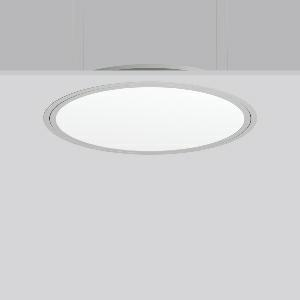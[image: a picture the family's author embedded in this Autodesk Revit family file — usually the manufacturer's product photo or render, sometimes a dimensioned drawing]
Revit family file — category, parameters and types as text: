
# Revit family: triona_round_e_312383_004_1_12_def9
name_source: partatom
category: Lighting Fixtures
units: mm (PartAtom-declared; Revit-internal decimal feet)

## family parameters
Cut with Voids When Loaded = No
Host = Face
Light Source = No
Part Type = Normal
Room Calculation Point = No
Round Connector Dimension = Use Diameter
Shared = No

## types (1)
- TRIONA round E (1 x LED Modul 840, 6750 lm, 4000)
    Apparent Load = 70 VA
    CIE Flux Codes = 49 80 96 100 100
    Color Rendering = 80
    Color Temperature = 4000
    Default Elevation = 1800 mm
    Description = Series: TRIONA round
Decorative round LED recessed surface luminaire. Cover made of sheet steel, powder-coated. Frame made of aluminium, powder-coated. Recessed ring: aluminium extrusion profile, powder coated. Light emission through a diffuser: plastic, opal. Lightguide and diffuser made of non-yellowing plastic (PMMA). Lateral light emission (RZB SIDELITE technology) for above-average homogeneous light distribution. Suitable for installation in cavity ceilings. Tool-free mounting system thanks to the rocker arm mechanism (patent pending). Electronic ballast included. Very easy installation thanks to Plug+Play connection. 
Colour: silver, matt (approx. RAL 9006)
Diameter: 725 mm
Height: 2 mm
Cut-out diameter: 702 mm
Recess height: 100 mm
Luminaire: recess height: 89 mm
Lamp: LED
Socket: without socket
Colour temperature: 4000K
Colour rendering index (CRI): 80
System power: 70 W
Rated luminous flux: 6750 lm
Luminous efficiency: 96 lm/W
Control gear: Converter, dimmable, DALI
Protection class: I
Type of protection: IP 40
    Height = 0 mm  [stored 0 ft]
    Lamp = 1 x LED Modul 840
    Lamp Light Flux = 6750 lm
    Lamp count = 1
    Length = 725 mm
    Lifetime = 50000 h
    Luminous efficacy = 96 lm/W
    Manufacturer = RZB
    ModVariant = No
    Model = 312383.004.1.12
    Mounting Place = Ceiling
    Mounting Type = Recessed
    Number of Poles = 1
    OnlyDefault = Yes
    Power Factor = 1
    Product Name = TRIONA round E
    Product group = Recessed modular luminaires
    ProductGroupID = 406
    Protection Class = Protection class I
    Protection Degree = IP 20
    RLX_Detail_Level = 1
    RLX_Emergency_Light_Flux = 0 lm
    RLX_Emergency_Type = 0
    RLX_Emergency_Type_DB = No
    RlxData = <blob elided: 36065 chars, md5=53a0ba45>
    Socket = socket
    Standby Power = 0 W
    System Light Flux = 6750 lm
    System Power = 70 W
    Type Comments = Product without accessories
    Type Image = 312383.004.12.jpg
    URL = http://relux.com
    VarID = ---
    Voltage = 230 V
    Voltage Range = 220-240 V
    Weight = 0.00 kg
    Width = 0 mm  [stored 0 ft]

note: [stored X ft] marks values corroborated as IEEE doubles in the binary element streams (Revit-internal decimal feet)

## geometry (parser evidence)
native form markers: Blend x4, Sweep x10
no freeform markers — native parametric forms only
